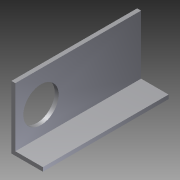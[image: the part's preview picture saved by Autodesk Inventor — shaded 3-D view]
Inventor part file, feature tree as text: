
AUTODESK INVENTOR PART (.ipt)
format: ipt  version: 2012 (Build 160160000, 160)  size: 87,552 bytes
history: native  units: in
note: dims shown in document units (in); Inventor stores cm internally (conversion verified against a paired STEP export)
features: extrude x2, sketch x2
ambient origin geometry x8: Origin, YZ Plane, XZ Plane, XY Plane, X Axis, Y Axis, Z Axis, Center Point
bodies: Solid1 (feature_tree)
feature tree (4):
  extrude  "Extrusion1"  Depth=1.0in
  extrude  "Extrusion2"  Depth=0.125in
  sketch  "Sketch1"  dims[d0=2.0in d1=1.0in]
  sketch  "Sketch2"  dims[d2=0.125in d3=0.125in d4=4.0in d5=0.0in d6=1.125in d7=3.1843in d8=1.0in d9=4.0in d10=0.0in]
